# Revit family: 4705
name_source: partatom
category: Plumbing Fixtures
units: mm (PartAtom-declared; Revit-internal decimal feet)

## family parameters
Cut with Voids When Loaded = No
Host = Face
OmniClass Number = 23.65.70.11.11
OmniClass Title = Fixtures for Liquids
Part Type = Normal
Room Calculation Point = No
Round Connector Dimension = Use Diameter
Shared = No

## types (2) — shared parameters
CW Connection = No
Gallons Per Minute = 0.000 GPM
HW Connection = No
Vent Connection = No
Waste Connection = No
z GPM GPM = 0.000 GPM
z Has .5 Inch Female Connections = Yes
z Has 1.5 GPM Flow Restrictor = Yes
z Has 2.0 GPM Flow Restrictor = Yes
z Has Check Stops = Yes
z Has Integral Service Stops = Yes
z Has Rebuild Kit Trim Only = No
z Has Reverse Core = Yes
z Has Showerhead = Yes
z Has Slip On Tub Spout = Yes
z Has Trim = No
z Has Volume Control = Yes
z Has Wide Lever Handle = Yes
z Visibility = Yes
zero-valued in all types: Default Elevation, z  Showerhead, z .5 Inch Female Connections, z Error Box Depth, z Error Box Height, z Error Box Width, z Flow Rate, z GPM Number, z Integral Service Stops, z Offset, z Overall Depth, z Overall Height, z Overall Width, z Pipe Radius, z Reverse Core, z Slip On Tub, z Type, z Type Finish, z Type GPM, z Type Model, z Wide Lever

## per-type parameters (varying)
| type | Product Material |
| Chrome | Chrome - Symmons - Polished |
| Satin Nickel | Nickel - Symmons - Satin |

## geometry (parser evidence)
native form markers: Blend x12, Sweep x11
no freeform markers — native parametric forms only
